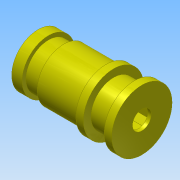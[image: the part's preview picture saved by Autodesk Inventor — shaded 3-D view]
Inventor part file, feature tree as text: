
AUTODESK INVENTOR PART (.ipt)
format: ipt  version: 2015 (Build 190159000, 159)  size: 204,288 bytes
history: native  units: mm
features: other x6, sketch x3, revolve x2, extrude x2, projected_geometry x2, fillet x1
ambient origin geometry x7: Origin, Ursprung, XZ Plane, XY Plane, X Axis, Y Axis, Z Axis
bodies: Volumenkörper1 (feature_tree)
feature tree (16):
  revolve  "Umdrehung1"
  other  "Nut für Sicherungsring2"
  other  "Nut für Sicherungsring1"
  revolve  "Umdrehung2"
  extrude  "Extrusion1"  Depth=14.0mm
  extrude  "Extrusion2"  Depth=8.445mm
  fillet  "Rundung1"  Radius=8.445mm
  other  "Startebene"
  other  "Hauptskizze"
  other  "iFeature27:1"
  other  "iFeature27:2"
  sketch  "Skizze3"  dims[d0=0.0mm d1=0.0mm d2=0.0mm d3=14.0mm]
  sketch  "Skizze4"  dims[d5=0.0mm d14=16.0mm d18=8.445mm]
  projected_geometry  "Projizierte Kontur1"
  projected_geometry  "Projizierte Kontur2"
  sketch  "Skizze5"  dims[d20=10.0mm d21=90.0deg d24=7.5mm d25=0.0mm d28=8.2mm d29=8.2mm d30=1.3mm d31=1.3mm d32=1.3mm d33=1.3mm d34=1.3mm d35=1.3mm d36=1.3mm d37=1.3mm d38=5.0mm d39=10.0mm d40=0.0mm d41=0.01mm]
